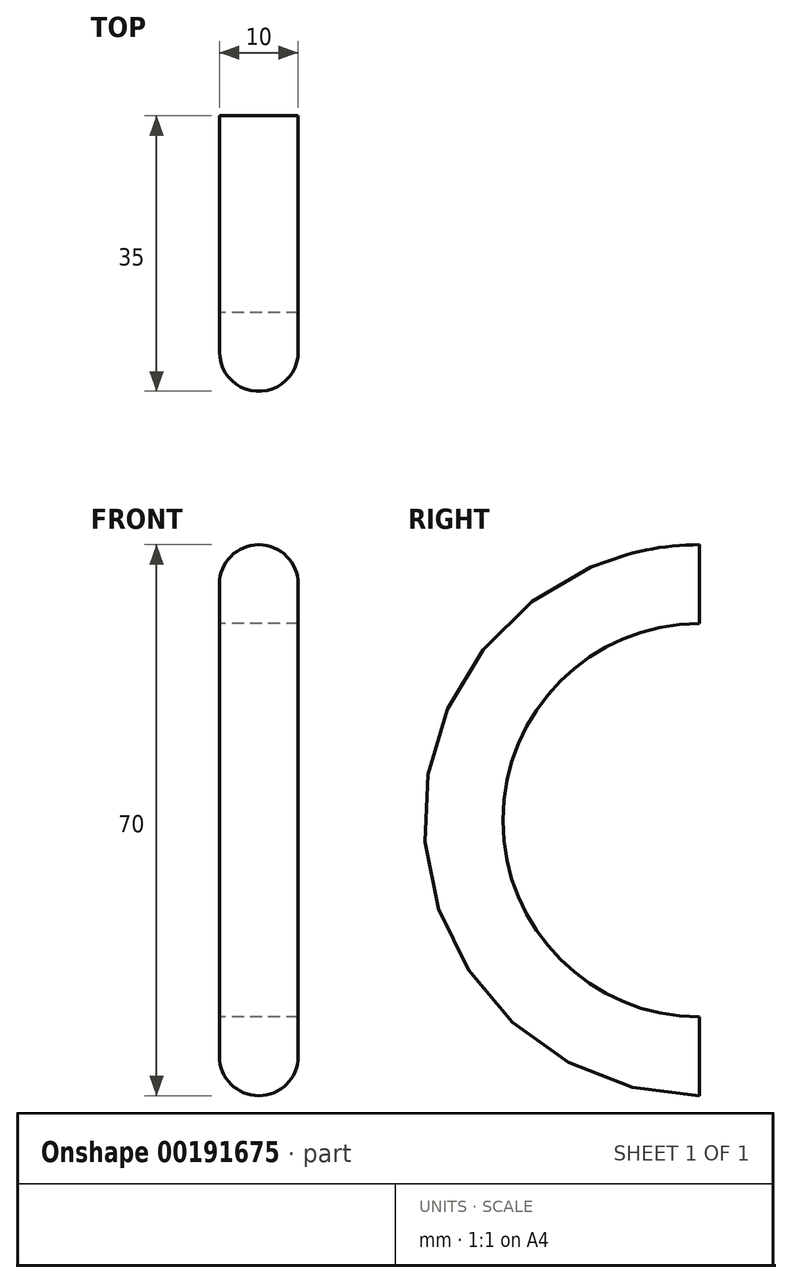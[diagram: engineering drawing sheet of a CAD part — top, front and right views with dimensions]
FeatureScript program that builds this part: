
annotation { "Feature Type Name" : "Feature", "Feature Type Description" : "" }
export const myFeature = defineFeature(function(context is Context, id is Id, definition is map)
    precondition{}
    {
        {
            var Q0;
            Q0=qCreatedBy(makeId("Right.planeOp"),FACE);
            var sketch = newSketch(context, id + "F0", { "sketchPlane" : qUnion([Q0])});
            skArc(sketch, "E0", {"start": v(0, 25) * mm, "mid": v(-25, 0) * mm, "end": v(0, -25) * mm});
            skArc(sketch, "E1.0", {"start": v(0, 35) * mm, "mid": v(-35, 0) * mm, "end": v(0, -35) * mm});
            skLineSegment(sketch, "E2", {"start": v(0, 35) * mm, "end": v(0, 25) * mm});
            skLineSegment(sketch, "E3", {"start": v(0, -25) * mm, "end": v(0, -35) * mm});
            skSolve(sketch);
        }
        {
            var Q0;
            Q0 = qSketchRegion(id + "F0", true);
            extrude(context, id + "F1", {"entities" : qUnion([Q0]), "depth" : 10 * mm});
        }
        {
            var Q0;
            Q0=makeQuery(id+"F1.opExtrude","CAP_EDGE",EDGE,{"disambiguationData":[OSD([sQuery(id+"F0.wireOp",EDGE,"E1.0")])],"isStart":true});
            var Q1;
            Q1=makeQuery(id+"F1.opExtrude","CAP_EDGE",EDGE,{"disambiguationData":[OSD([sQuery(id+"F0.wireOp",EDGE,"E1.0")])],"isStart":false});
            fillet(context, id + "F2", {"entities" : qUnion([Q0, Q1]), "radius" : 5 * mm, "tangentPropagation" : true, "allowEdgeOverflow" : false});
        }
    });
